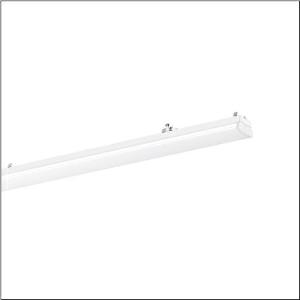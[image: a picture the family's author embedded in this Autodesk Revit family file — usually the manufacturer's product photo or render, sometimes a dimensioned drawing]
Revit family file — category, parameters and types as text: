
# Revit family: licross_r__21_recessed_opal_mo_52tl1ddn445g_2a2a
name_source: partatom
category: Lighting Fixtures
units: mm (PartAtom-declared; Revit-internal decimal feet)

## family parameters
Cut with Voids When Loaded = No
Host = Face
Light Source = No
Part Type = Normal
Room Calculation Point = No
Round Connector Dimension = Use Diameter
Shared = No

## types (1)
- --- (1 x LED, 4500 lm, 25.8 W, 4000K)
    Apparent Load = 26 VA
    CIE Flux Codes = 44 73 91 87 100
    Color Rendering = 80
    Color Temperature = 4000K
    Default Elevation = 1800 mm
    Description = Licross® 21 recessed opal MO, luminaire insert, of sheet steel, galvanised, coil coated, white, length: 1.500mm, width: 66mm, height: 67mm, LED rated luminous flux: 4.500lm, light colour: 840, control gear: DALI 2, with plug, 5-pole, with phase selection, mains connection: 220..240V, AC, 50/60Hz, rated input power: 26W, halogen-free wiring, primary optical cover: cover, of PMMA, light emission: direct with ceiling illumination distribution, primary light characteristic: symmetric, protection rating (complete): IP40, insulation class (complete): insulation class I (protective earthing), certification: CE, ENEC, VDE, UKCA, protection symbol: D if used in an environment without relevant dust loads with corresponding accessories, impact resistance: IK06, permissible ambient temperature for indoor applications: -25..+45°C, corresponds to IFS (International Featured Standards) requirements for safety and quality in the food industry, reducing of maximum allowable ambient temperature of 5°C with ceiling mounting, LABS conformity tested according to VDMA 24364:2018-05, packaging unit: 1 piece
    Height = 83 mm
    Lamp = 1 x LED
    Lamp Light Flux = 4500 lm
    Lamp Power = 25.8 W
    Lamp count = 1
    Length = 1500 mm
    Luminous efficacy = 174 lm/W
    Manufacturer = Siteco
    ModVariant = No
    Model = 52TL1DDN445G
    Mounting Place = Ceiling
    Mounting Type = Pendant
    Number of Poles = 1
    OnlyDefault = Yes
    Power Factor = 1
    Product Name = Licross® 21 recessed opal MO
    Product group = luminaire insert
    ProductGroupID = 901
    Protection Class = Protection class I
    Protection Degree = IP 40
    RLX_Detail_Level = 1
    RLX_Emergency_Light_Flux = 0 lm
    RLX_Emergency_Type = 0
    RLX_Emergency_Type_DB = No
    RlxData = <blob elided: 26313 chars, md5=25568474>
    Socket = socket
    Standby Power = 0 W
    System Light Flux = 4500 lm
    System Power = 26 W
    Type Comments = factory setting: luminous flux: 100 % | dim-lin: 254 | 172 mA
    Type Image = l_1313666.jpg
    URL = http://relux.com
    VarID = @adj_022369
    Voltage = 0 V
    Weight = 0.00 kg
    Width = 76 mm

## geometry (parser evidence)
native form markers: Blend x4, Sweep x14
no freeform markers — native parametric forms only
